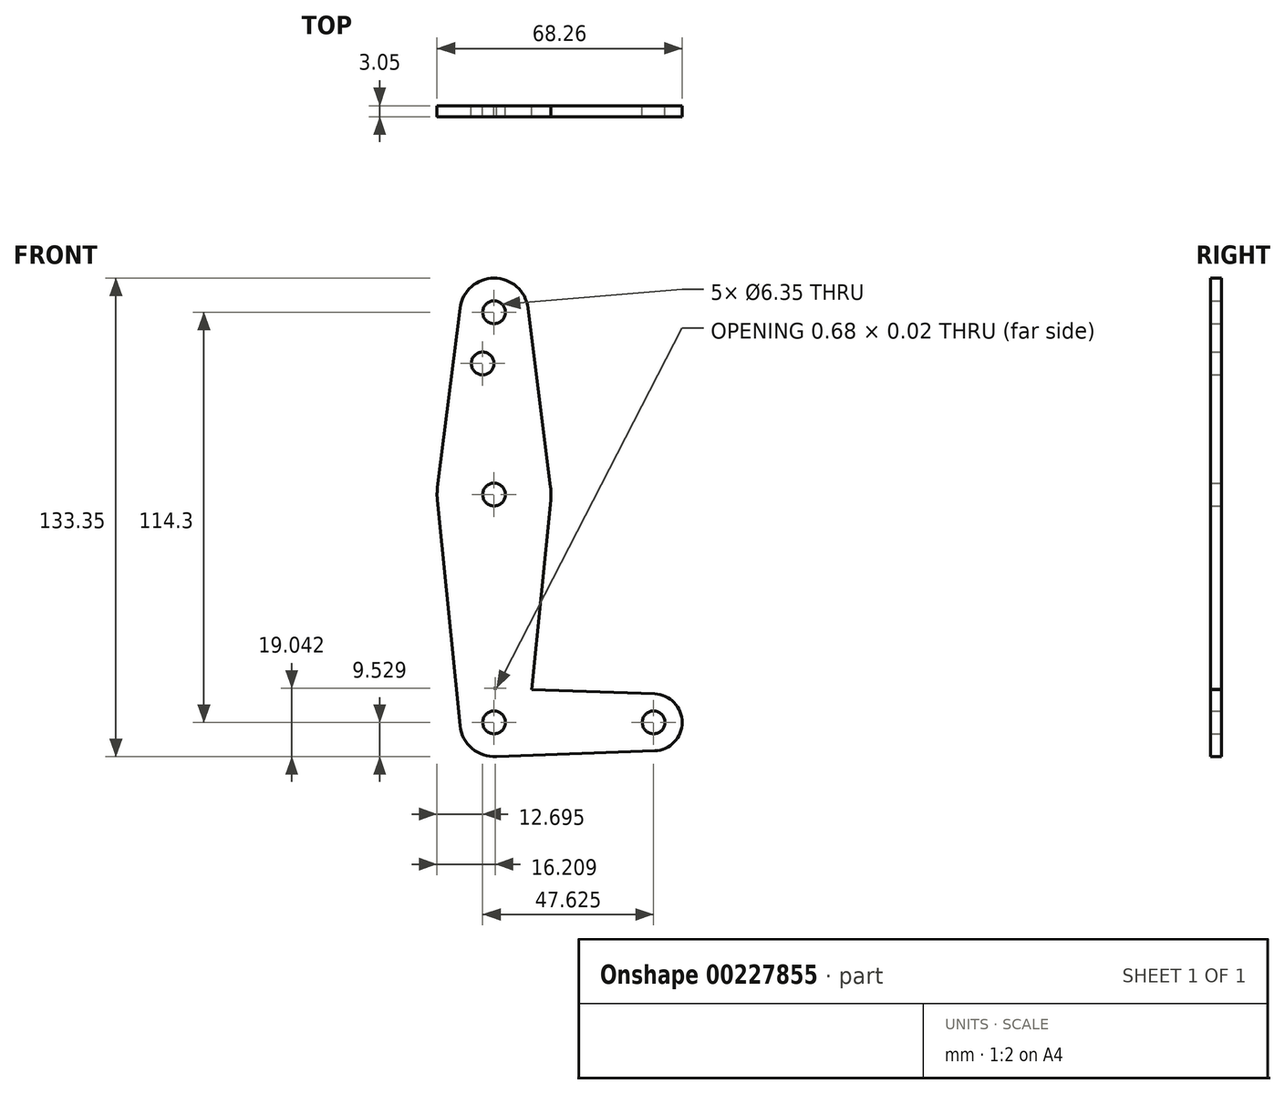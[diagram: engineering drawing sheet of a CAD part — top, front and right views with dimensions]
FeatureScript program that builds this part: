
annotation { "Feature Type Name" : "Feature", "Feature Type Description" : "" }
export const myFeature = defineFeature(function(context is Context, id is Id, definition is map)
    precondition{}
    {
        {
            var Q0;
            Q0=qCreatedBy(makeId("Front.planeOp"),FACE);
            var sketch = newSketch(context, id + "F0", { "sketchPlane" : qUnion([Q0])});
            skLineSegment(sketch, "E0", {"start": v(0, -50.36) * mm, "end": v(44.45, -50.36) * mm, "construction": true});
            skCircle(sketch, "E1", {"center": v(0, 63.94) * mm, "radius": 9.53 * mm});
            skCircle(sketch, "E2", {"center": v(0, -50.36) * mm, "radius": 9.53 * mm});
            skCircle(sketch, "E3", {"center": v(44.45, -50.36) * mm, "radius": 7.94 * mm});
            skCircle(sketch, "E4", {"center": v(0, 13.14) * mm, "radius": 15.88 * mm});
            skLineSegment(sketch, "E5", {"start": v(-9.45, 65.13) * mm, "end": v(-15.75, 15.12) * mm});
            skLineSegment(sketch, "E6", {"start": v(9.45, 65.13) * mm, "end": v(15.75, 15.12) * mm});
            skLineSegment(sketch, "E7", {"start": v(-15.8, 11.55) * mm, "end": v(-9.48, -51.31) * mm});
            skLineSegment(sketch, "E8", {"start": v(15.8, 11.55) * mm, "end": v(9.48, -51.31) * mm});
            skLineSegment(sketch, "E9", {"start": v(0, -40.84) * mm, "end": v(44.73, -42.43) * mm});
            skLineSegment(sketch, "E10", {"start": v(0, -59.89) * mm, "end": v(44.73, -58.3) * mm});
            skCircle(sketch, "E11", {"center": v(0, 13.14) * mm, "radius": 3.18 * mm});
            skCircle(sketch, "E12", {"center": v(-3.17, 49.66) * mm, "radius": 3.18 * mm});
            skLineSegment(sketch, "E13", {"start": v(0, 63.94) * mm, "end": v(0, -50.36) * mm, "construction": true});
            skCircle(sketch, "E14", {"center": v(0, -50.36) * mm, "radius": 3.18 * mm});
            skCircle(sketch, "E15", {"center": v(44.45, -50.36) * mm, "radius": 3.18 * mm});
            skCircle(sketch, "E16", {"center": v(0, 63.94) * mm, "radius": 3.18 * mm});
            skSolve(sketch);
        }
        {
            var Q0;
            Q0 = qSketchRegion(id + "F0", true);
            extrude(context, id + "F1", {"entities" : qUnion([Q0]), "depth" : 3.05 * mm});
        }
    });
